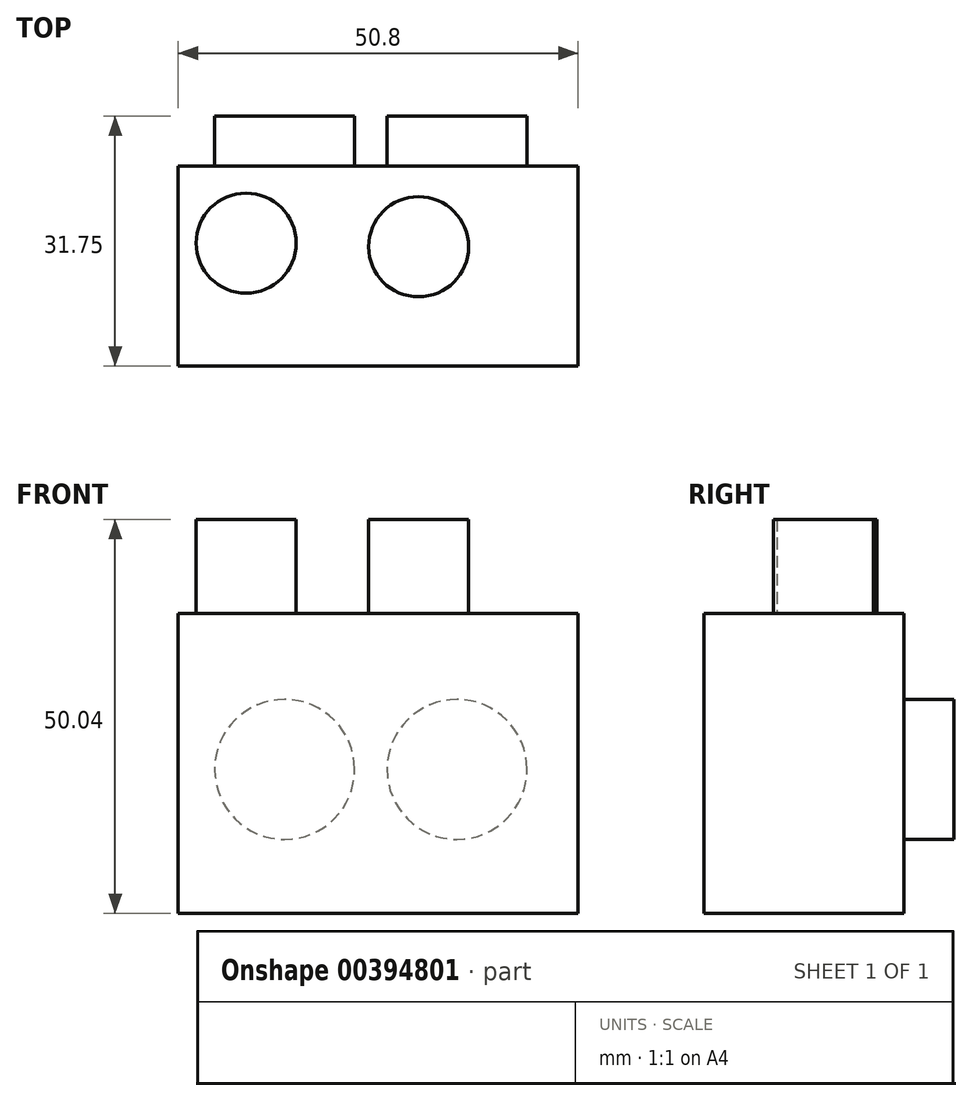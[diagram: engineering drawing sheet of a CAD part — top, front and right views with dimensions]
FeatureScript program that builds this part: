
annotation { "Feature Type Name" : "Feature", "Feature Type Description" : "" }
export const myFeature = defineFeature(function(context is Context, id is Id, definition is map)
    precondition{}
    {
        {
            var Q0;
            Q0=qCreatedBy(makeId("Front.planeOp"),FACE);
            var sketch = newSketch(context, id + "F0", { "sketchPlane" : qUnion([Q0])});
            skLineSegment(sketch, "E0.bottom", {"start": v(0, 0) * mm, "end": v(-50.8, 0) * mm});
            skLineSegment(sketch, "E0.top", {"start": v(0, -38.1) * mm, "end": v(-50.8, -38.1) * mm});
            skLineSegment(sketch, "E0.left", {"start": v(0, 0) * mm, "end": v(0, -38.1) * mm});
            skLineSegment(sketch, "E0.right", {"start": v(-50.8, 0) * mm, "end": v(-50.8, -38.1) * mm});
            skSolve(sketch);
        }
        {
            var Q0;
            Q0 = qSketchRegion(id + "F0", true);
            extrude(context, id + "F1", {"entities" : qUnion([Q0]), "depth" : 25.4 * mm});
        }
        {
            var Q0;
            Q0=qCreatedBy(makeId("Top.planeOp"),FACE);
            var sketch = newSketch(context, id + "F2", { "sketchPlane" : qUnion([Q0])});
            skCircle(sketch, "E1", {"center": v(-42.17, -9.78) * mm, "radius": 6.35 * mm});
            skCircle(sketch, "E2", {"center": v(-20.27, -10.25) * mm, "radius": 6.35 * mm});
            skSolve(sketch);
        }
        {
            var Q0;
            Q0 = qSketchRegion(id + "F2", true);
            extrude(context, id + "F3", {"entities" : qUnion([Q0]), "operationType" : NewBodyOperationType.ADD, "depth" : 11.94 * mm});
        }
        {
            var Q0;
            Q0=qCreatedBy(makeId("Front.planeOp"),FACE);
            var sketch = newSketch(context, id + "F4", { "sketchPlane" : qUnion([Q0])});
            skCircle(sketch, "E3", {"center": v(-15.38, -19.8) * mm, "radius": 8.9 * mm});
            skCircle(sketch, "E4", {"center": v(-37.27, -19.8) * mm, "radius": 8.9 * mm});
            skSolve(sketch);
        }
        {
            var Q0;
            Q0 = qSketchRegion(id + "F4", true);
            extrude(context, id + "F5", {"entities" : qUnion([Q0]), "operationType" : NewBodyOperationType.ADD, "oppositeDirection" : true, "depth" : 6.35 * mm});
        }
    });
